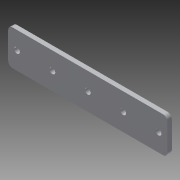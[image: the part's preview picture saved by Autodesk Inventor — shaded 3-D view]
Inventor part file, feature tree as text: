
AUTODESK INVENTOR PART (.ipt)
format: ipt  version: 2014 (Build 180170000, 170)  size: 92,160 bytes
history: native  units: in
note: dims shown in document units (in); Inventor stores cm internally (conversion verified against a paired STEP export)
features: extrude x1, fillet x1, sketch x1
ambient origin geometry x8: Origin, YZ Plane, XZ Plane, XY Plane, X Axis, Y Axis, Z Axis, Center Point
bodies: Solid1 (feature_tree)
feature tree (3):
  extrude  "Extrusion1"  Depth=1.0in
  fillet  "Fillet1"  Radius=0.163in
  sketch  "Sketch1"  dims[d0=4.5in d1=1.0in d2=0.163in d3=0.25in d4=0.5in d12=0.125in d13=0.0in d14=0.125in d15=1.9685in d17=1.0in d18=0.3937in d20=1.0in]
